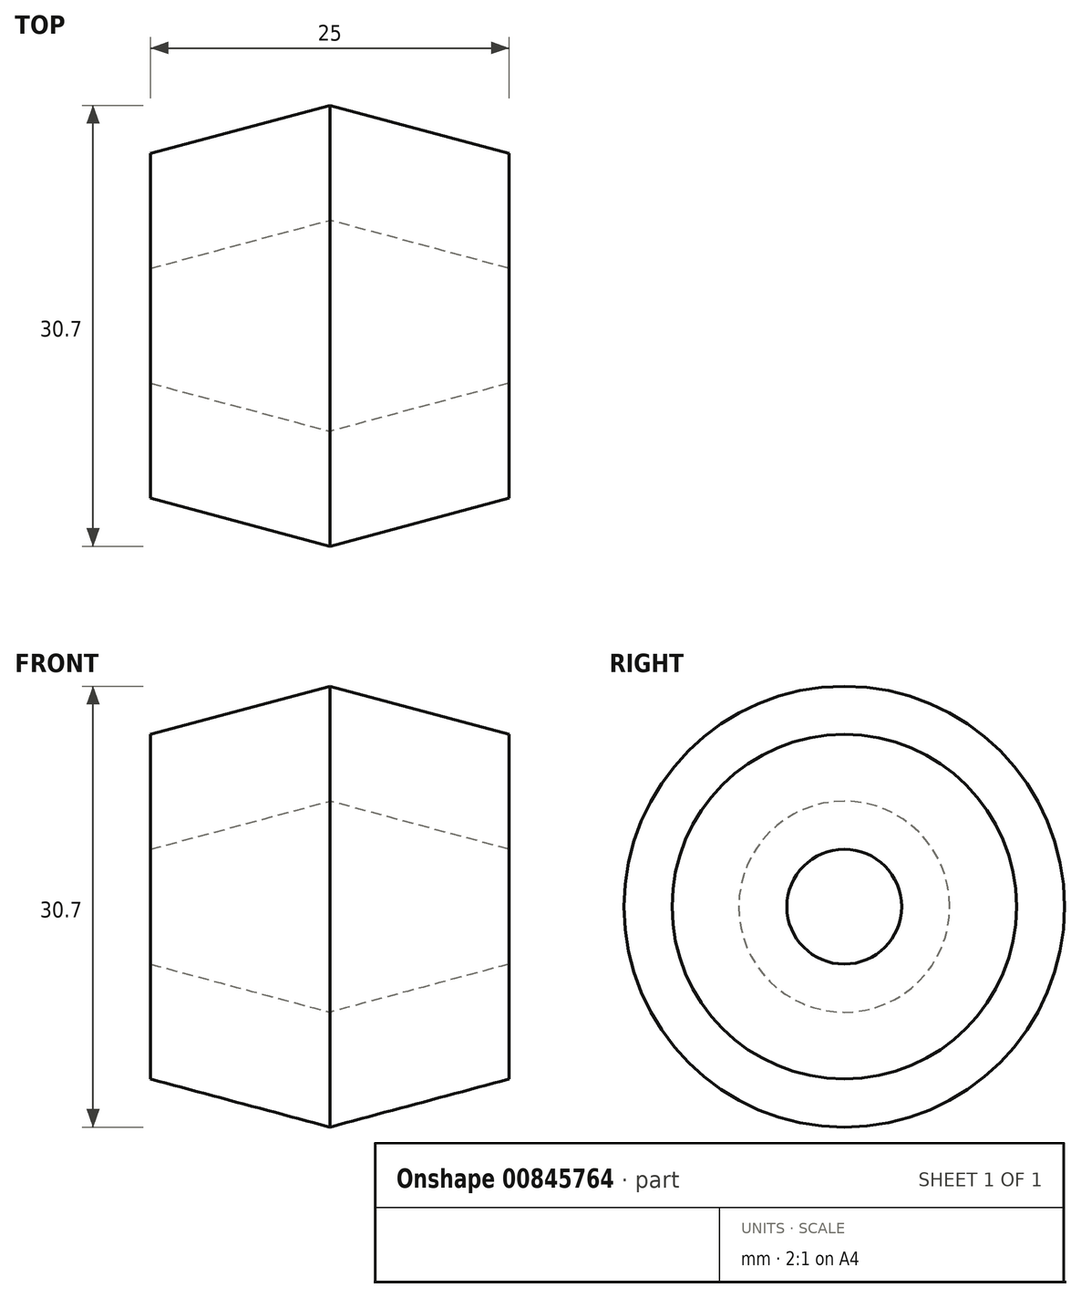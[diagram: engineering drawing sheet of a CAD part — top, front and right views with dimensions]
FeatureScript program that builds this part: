
annotation { "Feature Type Name" : "Feature", "Feature Type Description" : "" }
export const myFeature = defineFeature(function(context is Context, id is Id, definition is map)
    precondition{}
    {
        {
            var Q0;
            Q0=qCreatedBy(makeId("Front.planeOp"),FACE);
            var sketch = newSketch(context, id + "F0", { "sketchPlane" : qUnion([Q0])});
            skLineSegment(sketch, "E0", {"start": v(0, 0) * mm, "end": v(0, -8) * mm});
            skLineSegment(sketch, "E1", {"start": v(0, -8) * mm, "end": v(-12.5, -11.35) * mm});
            skLineSegment(sketch, "E2", {"start": v(-12.5, -11.35) * mm, "end": v(-25, -8) * mm});
            skLineSegment(sketch, "E3", {"start": v(-25, -8) * mm, "end": v(-25, 0) * mm});
            skLineSegment(sketch, "E4", {"start": v(-25, 0) * mm, "end": v(-12.5, -3.35) * mm});
            skLineSegment(sketch, "E5", {"start": v(-12.5, -3.35) * mm, "end": v(0, 0) * mm});
            skLineSegment(sketch, "E6", {"start": v(-26.91, 4) * mm, "end": v(3.77, 4) * mm, "construction": true});
            skSolve(sketch);
        }
        {
            var Q0;
            Q0=sQuery(id+"F0.wireOp",EDGE,"E6");
            var Q1;
            Q1=sQuery(id+"F0.wireOp",EDGE,"E4");
            var Q2;
            Q2=sQuery(id+"F0.wireOp",EDGE,"E3");
            var Q3;
            Q3=sQuery(id+"F0.wireOp",EDGE,"E2");
            var Q4;
            Q4=sQuery(id+"F0.wireOp",EDGE,"E1");
            var Q5;
            Q5=sQuery(id+"F0.wireOp",EDGE,"E0");
            var Q6;
            Q6=sQuery(id+"F0.wireOp",EDGE,"E5");
            var Q7;
            Q7=sQuery(id+"F0.wireOp",EDGE,"E6");
            revolve(context, id + "F1", {"bodyType" : ToolBodyType.SURFACE, "surfaceOperationType" : NewSurfaceOperationType.NEW, "surfaceEntities" : qUnion([Q0, Q1, Q2, Q3, Q4, Q5, Q6]), "axis" : qUnion([Q7]), "revolveType" : RevolveType.FULL});
        }
    });
